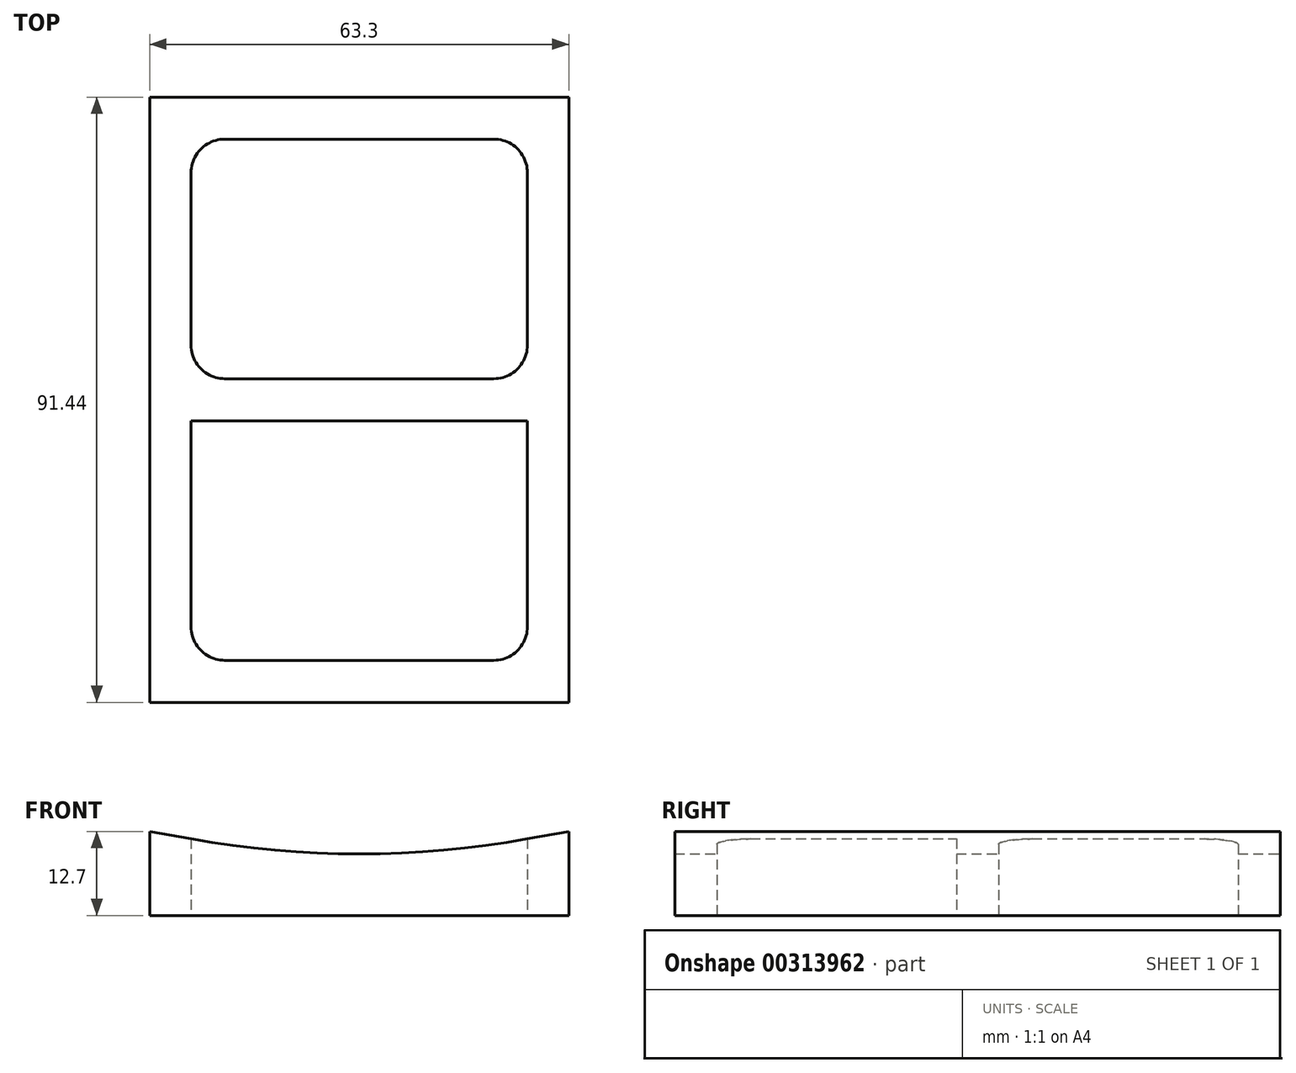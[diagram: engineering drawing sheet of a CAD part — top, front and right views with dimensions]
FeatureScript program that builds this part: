
annotation { "Feature Type Name" : "Feature", "Feature Type Description" : "" }
export const myFeature = defineFeature(function(context is Context, id is Id, definition is map)
    precondition{}
    {
        {
            var Q0;
            Q0=qCreatedBy(makeId("Front.planeOp"),FACE);
            var sketch = newSketch(context, id + "F0", { "sketchPlane" : qUnion([Q0])});
            skLineSegment(sketch, "E0", {"start": v(0, 42.8) * mm, "end": v(0, 9.28) * mm});
            skLineSegment(sketch, "E1", {"start": v(-25.4, 42.8) * mm, "end": v(25.4, 42.8) * mm});
            skPoint(sketch, "E2", {"position": v(0, 42.8) * mm});
            skLineSegment(sketch, "E3", {"start": v(25.4, 11.57) * mm, "end": v(25.4, 42.8) * mm});
            skLineSegment(sketch, "E4.MirrorCS", {"start": v(-25.4, 11.57) * mm, "end": v(-25.4, 42.8) * mm});
            skArc(sketch, "E5", {"start": v(25.4, 11.57) * mm, "mid": v(0, 9.28) * mm, "end": v(-25.4, 11.57) * mm});
            skLineSegment(sketch, "E6", {"start": v(-25.4, 11.57) * mm, "end": v(-31.65, 12.7) * mm});
            skLineSegment(sketch, "E7.MirrorCS", {"start": v(25.4, 11.57) * mm, "end": v(31.65, 12.7) * mm});
            skLineSegment(sketch, "E8", {"start": v(-31.65, 12.7) * mm, "end": v(-31.65, 0) * mm});
            skLineSegment(sketch, "E9", {"start": v(-31.65, 0) * mm, "end": v(31.65, 0) * mm});
            skLineSegment(sketch, "E10", {"start": v(31.65, 0) * mm, "end": v(31.65, 12.7) * mm});
            skPoint(sketch, "E11", {"position": v(0, 0) * mm});
            skLineSegment(sketch, "E12", {"start": v(-25.4, 11.57) * mm, "end": v(-25.4, 0) * mm});
            skLineSegment(sketch, "E13.MirrorCS", {"start": v(25.4, 11.57) * mm, "end": v(25.4, 0) * mm});
            skSolve(sketch);
        }
        {
            var Q0;
            {var subQ0=sQuery(id+"F0.wireOp",EDGE,"E12");Q0=makeQuery(id+"F0.imprint","IMPRINT",FACE,{"disambiguationData":[TD([[makeQuery(id+"F0.imprint","IMPRINT",EDGE,{"derivedFrom":subQ0}),1.0]])]});}
            var Q1;
            Q1=makeQuery(id+"F0.imprint","IMPRINT",FACE,{"disambiguationData":[TD([[makeQuery(id+"F0.imprint","IMPRINT",EDGE,{"derivedFrom":sQuery(id+"F0.wireOp",EDGE,"E6")}),1.0]])]});
            var Q2;
            Q2=makeQuery(id+"F0.imprint","IMPRINT",FACE,{"disambiguationData":[TD([[makeQuery(id+"F0.imprint","IMPRINT",EDGE,{"derivedFrom":sQuery(id+"F0.wireOp",EDGE,"E7.MirrorCS")}),-1.0]])]});
            extrude(context, id + "F1", {"entities" : qUnion([Q0, Q1, Q2]), "endBound" : BoundingType.SYMMETRIC, "depth" : 91.44 * mm});
        }
        {
            var Q0;
            {var subQ0=sQuery(id+"F0.wireOp",EDGE,"E12");Q0=makeQuery(id+"F0.imprint","IMPRINT",FACE,{"disambiguationData":[TD([[makeQuery(id+"F0.imprint","IMPRINT",EDGE,{"derivedFrom":subQ0}),1.0]])]});}
            extrude(context, id + "F2", {"entities" : qUnion([Q0]), "operationType" : NewBodyOperationType.REMOVE, "endBound" : BoundingType.SYMMETRIC, "depth" : 78.74 * mm});
        }
        {
            var Q0;
            {var subQ0=sQuery(id+"F0.wireOp",EDGE,"E12");Q0=makeQuery(id+"F0.imprint","IMPRINT",FACE,{"disambiguationData":[TD([[makeQuery(id+"F0.imprint","IMPRINT",EDGE,{"derivedFrom":subQ0}),1.0]])]});}
            extrude(context, id + "F3", {"entities" : qUnion([Q0]), "operationType" : NewBodyOperationType.ADD, "endBound" : BoundingType.SYMMETRIC, "depth" : 6.35 * mm});
        }
        {
            var Q0;
            Q0=makeQuery(id+"F2.boolean.opBoolean","COPY",EDGE,{"derivedFrom":makeQuery(id+"F2.opExtrude","CAP_EDGE",EDGE,{"disambiguationData":[OSD([sQuery(id+"F0.wireOp",EDGE,"E12")])],"isStart":true})});
            var Q1;
            Q1=makeQuery(id+"F2.boolean.opBoolean","COPY",EDGE,{"derivedFrom":makeQuery(id+"F2.opExtrude","CAP_EDGE",EDGE,{"disambiguationData":[OSD([sQuery(id+"F0.wireOp",EDGE,"E13.MirrorCS")])],"isStart":true})});
            var Q2;
            Q2=makeQuery(id+"F3.opExtrude","CAP_EDGE",EDGE,{"disambiguationData":[OSD([sQuery(id+"F0.wireOp",EDGE,"E13.MirrorCS")])],"isStart":false});
            var Q3;
            Q3=makeQuery(id+"F3.opExtrude","CAP_EDGE",EDGE,{"disambiguationData":[OSD([sQuery(id+"F0.wireOp",EDGE,"E12")])],"isStart":false});
            var Q4;
            Q4=makeQuery(id+"F3.opExtrude","CAP_EDGE",EDGE,{"disambiguationData":[OSD([sQuery(id+"F0.wireOp",EDGE,"E13.MirrorCS")])],"isStart":true});
            var Q5;
            Q5=makeQuery(id+"F2.boolean.opBoolean","COPY",EDGE,{"derivedFrom":makeQuery(id+"F2.opExtrude","CAP_EDGE",EDGE,{"disambiguationData":[OSD([sQuery(id+"F0.wireOp",EDGE,"E13.MirrorCS")])],"isStart":false})});
            var Q6;
            Q6=makeQuery(id+"F2.boolean.opBoolean","COPY",EDGE,{"derivedFrom":makeQuery(id+"F2.opExtrude","CAP_EDGE",EDGE,{"disambiguationData":[OSD([sQuery(id+"F0.wireOp",EDGE,"E12")])],"isStart":false})});
            var Q7;
            Q7=makeQuery(id+"F3.opExtrude","CAP_EDGE",EDGE,{"disambiguationData":[OSD([sQuery(id+"F0.wireOp",EDGE,"E12")])],"isStart":true});
            fillet(context, id + "F4", {"entities" : qUnion([Q0, Q1, Q2, Q3, Q4, Q5, Q6, Q7]), "radius" : 5.08 * mm, "tangentPropagation" : true, "allowEdgeOverflow" : false});
        }
    });
